# Revit family: TEMID_Шлагбаум_BGM1030R
name_source: partatom
category: Охранная сигнализация
units: mm (PartAtom-declared; Revit-internal decimal feet)

## family parameters
Всегда вертикально = Нет
На основе рабочей плоскости = Нет
Общий = Да
При загрузке вырезать с полостями = Нет
Размер круглого соединителя = Использовать диаметр
Сохранять ориентацию аннотаций = Нет
Тип детали = Нормальный
Точка расчета площади = Да

## types (4) — shared parameters
=Габариты= = =Габариты=
=Стрела= = =Стрела=
ADSK_Единица измерения = шт.
ADSK_Завод-изготовитель = TEMID
ADSK_Классификация нагрузок = Прочее
ADSK_Количество = 1
ADSK_Количество фаз = 1
ADSK_Коэффициент мощности = 0.95
ADSK_Напряжение = 220 В
ADSK_Номинальная мощность = 120 Вт
ADSK_Обозначение = RD
ADSK_Полная мощность = 126 В·А
ADSK_Раздел спецификации = 3. Периферийное оборудование
ADSK_Размер_Высота = 1010 мм
ADSK_Размер_Глубина = 280 мм
ADSK_Размер_Ширина = 350 мм
ADSK_Ток = 574.163 мА
URL = https://temid-global.ru
Зона обслуживания_Отступ от прибора = 250 мм
Материал боковины стрелы = Красный
Материал буквы_Стрела закрыта = Зеленый
Материал буквы_Стрела открыта = Красный
Материал стойки = Черный
Материал стрелы = Белый
Стрела основание_Высота = 150 мм
Стрела основание_Глубина = 50 мм
Стрела основание_Ширина = 150 мм
Стрела_Высота снования = 700 мм
Стрела_Глубина = 40 мм
Стрела_Длина общая = 3000 мм
Стрела_Ширина = 50 мм
УГО_Тип = УГО_СС_Универсальный_текст_прямоугольный : УГО_СС_Шлагбаум
Угол 2_открытой стрелы = 90.00°
zero-valued in all types: Отметка по умолчанию

## per-type parameters (varying)
| type | ADSK_Марка | ADSK_Наименование | ADSK_Тип | Стрела подъём Г образный | Стрела подъём стандартный | Стрела_Длина 1 участка | Стрела_Длина 2 участка | Стрела_Левая | Стрела_Правая | Угол 1_закрытой стрелы | Угол 1_открытой стрелы | Угол 2_закрытой стрелы |
| BGM1030R_Стрела_Правая_Подъём стандарт | BGM1030R | Шлагбаум электромеханический со стрелой 3.0м телескоп., бесщеточный двигатель,время подъема 5 c, 220В (120 Вт), с блоком управления, индикацией шлагбаума,  -35 ~ +70 град.С., правый, Bluetooth, APP ZKBarrier. | BGM1030R | Нет | Да | 30 мм | 2730 мм | Нет | Да | 90.00° | 180.00° | 90.00° |
| BGM1030L_Стрела_Левая_Подъём стандарт | BGM1030L | Шлагбаум электромеханический со стрелой 3.0м телескоп., бесщеточный двигатель,время подъема 5 c, 220В (120 Вт), с блоком управления, индикацией шлагбаума,  -35 ~ +70 град.С., левый, Bluetooth, APP ZKBarrier. | BGM1030L | Нет | Да | 30 мм | 2730 мм | Да | Нет | 270.00° | 180.00° | 90.00° |
| BGM1030L_Стрела_Левая_Подъём Г-образный | BGM1030L | Шлагбаум электромеханический со стрелой 3.0м телескоп., бесщеточный двигатель,время подъема 5 c, 220В (120 Вт), с блоком управления, индикацией шлагбаума,  -35 ~ +70 град.С., левый, Bluetooth, APP ZKBarrier. | BGM1030L | Да | Нет | 1500 мм | 1500 мм | Да | Нет | 180.00° | 270.00° | 180.00° |
| BGM1030R_Стрела_Правая_Подъём Г-образный | BGM1030R | Шлагбаум электромеханический со стрелой 3.0м телескоп., бесщеточный двигатель,время подъема 5 c, 220В (120 Вт), с блоком управления, индикацией шлагбаума,  -35 ~ +70 град.С., правый, Bluetooth, APP ZKBarrier. | BGM1030R | Да | Нет | 1500 мм | 1500 мм | Нет | Да | 180.00° | 90.00° | 0.00° |
